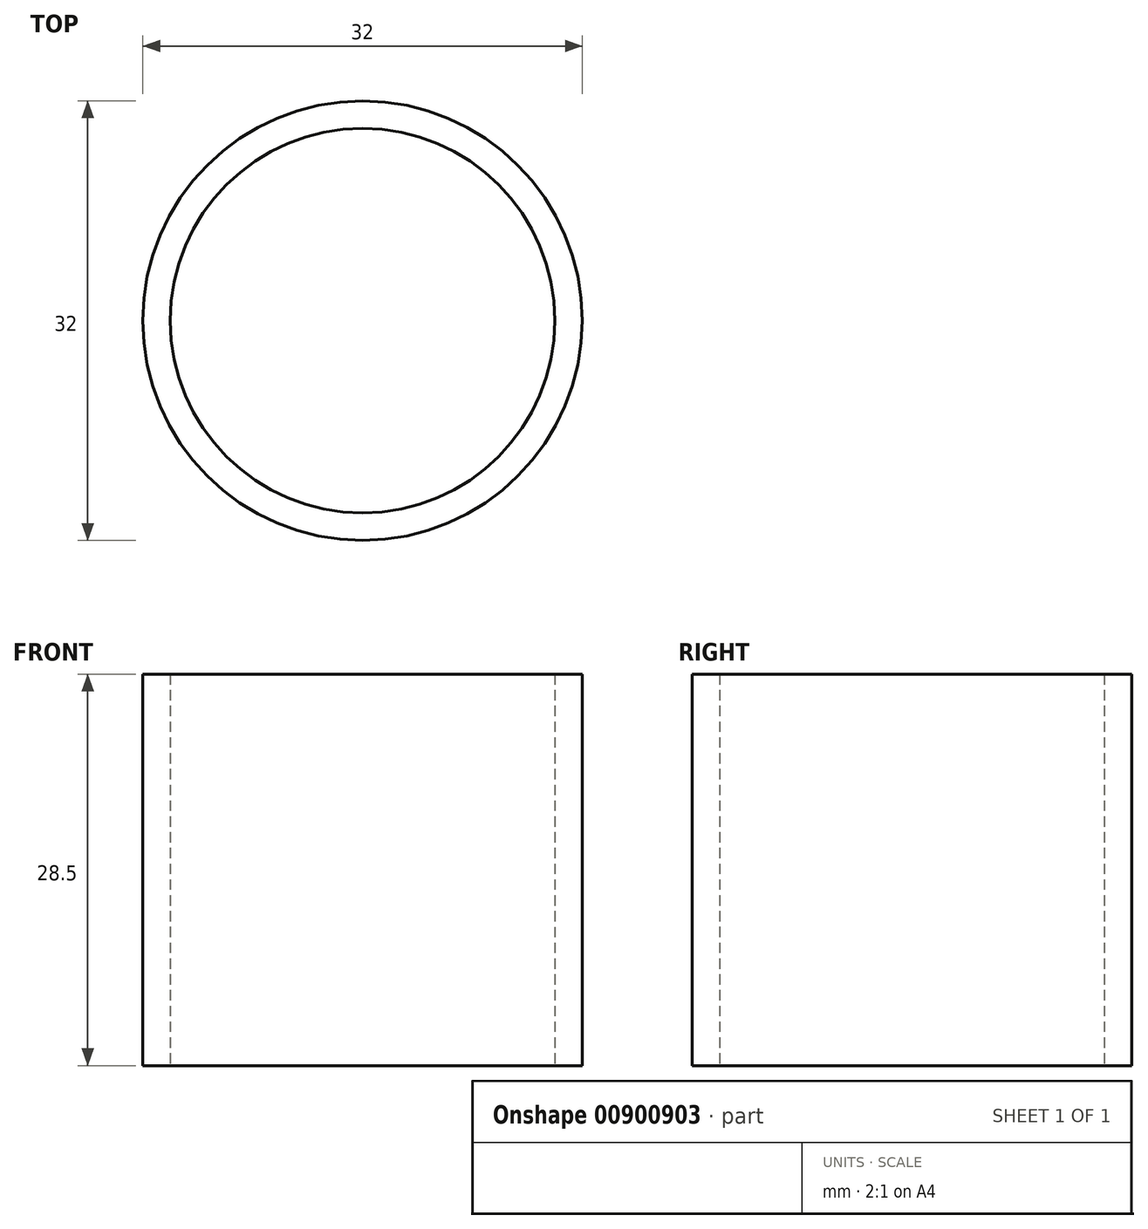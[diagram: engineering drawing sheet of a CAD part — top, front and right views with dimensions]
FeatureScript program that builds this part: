
annotation { "Feature Type Name" : "Feature", "Feature Type Description" : "" }
export const myFeature = defineFeature(function(context is Context, id is Id, definition is map)
    precondition{}
    {
        {
            var Q0;
            Q0=qCreatedBy(makeId("Top.planeOp"), FACE);
            var sketch = newSketch(context, id + "F0", { "sketchPlane" : qUnion([Q0])});
            skCircle(sketch, "E0", {"center": v(0, 0) * mm, "radius": 14 * mm});
            skCircle(sketch, "E1", {"center": v(0, 0) * mm, "radius": 16 * mm});
            skSolve(sketch);
        }
        {
            var Q0;
            Q0 = qSketchRegion(id + "F0", true);
            extrude(context, id + "F1", {"entities" : qUnion([Q0]), "depth" : 28.5 * mm, "offsetDistance" : 25 * mm});
        }
    });
